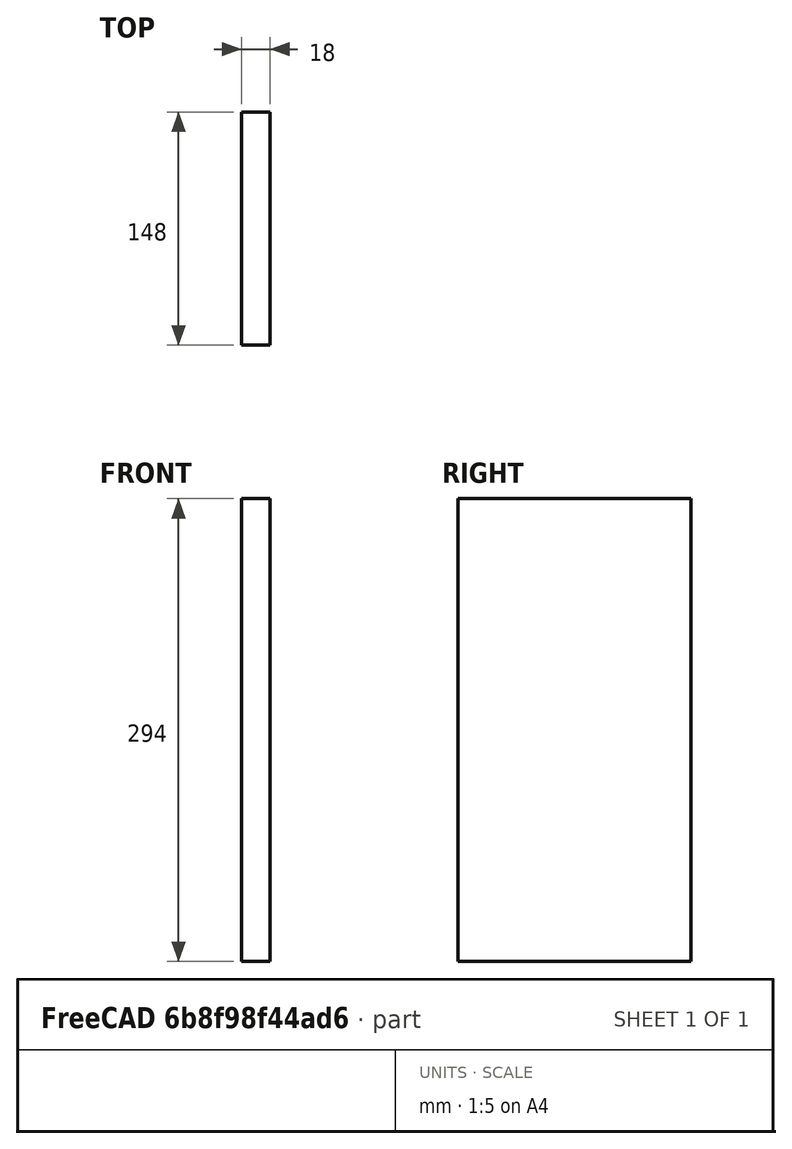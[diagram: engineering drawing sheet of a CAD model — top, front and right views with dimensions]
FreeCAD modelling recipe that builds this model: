
FCSTD DOCUMENT  (FreeCAD 0.17R13541 (Git))
Label: FaceLaterale
License: All rights reserved
LicenseURL: http://en.wikipedia.org/wiki/All_rights_reserved
objects: Sketcher::SketchObject×1, PartDesign::Pad×1, PartDesign::Body×1
note: 4 computed .brp shape members not serialized (recipe doc carries the construction recipe); baked Part::Feature solids carry a one-line shape summary decoded from their .brp

FEATURE [Sketcher::SketchObject] Sketch
  MapMode = 5
  Placement = pos=(0,0,0) rot=(0.57735,0.57735,0.57735;2.0944rad)
  Support = -> [YZ_Plane]
  sketch-geometry (6):
    g0: LineSegment StartX=-74 StartY=147 StartZ=0 EndX=74 EndY=147 EndZ=0
    g1: LineSegment StartX=74 StartY=147 StartZ=0 EndX=74 EndY=-147 EndZ=0
    g2: LineSegment StartX=74 StartY=-147 StartZ=0 EndX=-74 EndY=-147 EndZ=0
    g3: LineSegment StartX=-74 StartY=-147 StartZ=0 EndX=-74 EndY=147 EndZ=0
    g4: LineSegment [constr] StartX=-74 StartY=147 StartZ=0 EndX=74 EndY=-147 EndZ=0
    g5: LineSegment [constr] StartX=-74 StartY=-147 StartZ=0 EndX=74 EndY=147 EndZ=0
  constraints (16):
    c: Coincident(g0,g1)
    c: Coincident(g1,g2)
    c: Coincident(g2,g3)
    c: Coincident(g3,g0)
    c: Horizontal(g0)
    c: Horizontal(g2)
    c: Vertical(g1)
    c: Vertical(g3)
    c: Coincident(g4,g0)
    c: Coincident(g4,g1)
    c: Coincident(g5,g2)
    c: Coincident(g5,g0)
    c: PointOnObject(g-1,g4)
    c: PointOnObject(g-1,g5)
    c: DistanceX(g0,g0) = 148  'Profondeur b'
    c: DistanceY(g3,g3) = 294  'Hauteur C'
FEATURE [PartDesign::Pad] Pad
  Length = 18
  Length2 = 100
  Placement = pos=(0,0,0) rot=(0.57735,0.57735,0.57735;2.0944rad)
  Profile = -> Sketch
  Type = 0
FEATURE [PartDesign::Body] Body  label="Face laterale"
  Group = -> [Sketch,Pad]
  Origin = -> Origin
  Tip = -> Pad
